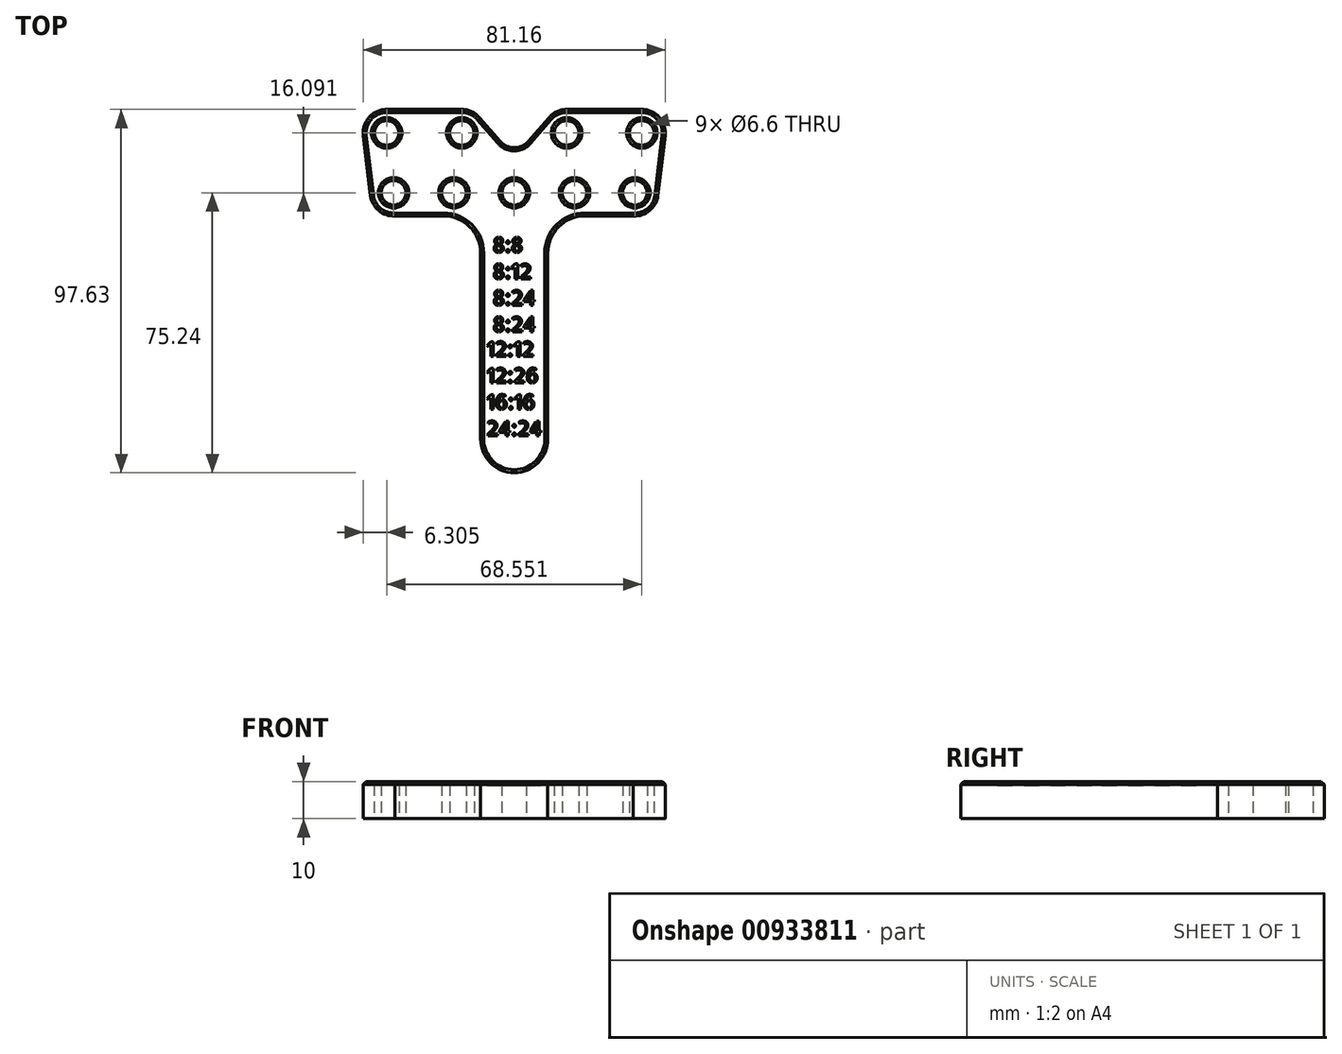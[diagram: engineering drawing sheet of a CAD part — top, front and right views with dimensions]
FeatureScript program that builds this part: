
annotation { "Feature Type Name" : "Feature", "Feature Type Description" : "" }
export const myFeature = defineFeature(function(context is Context, id is Id, definition is map)
    precondition{}
    {
        {
            var Q0;
            Q0=qCreatedBy(makeId("Top.planeOp"),FACE);
            var sketch = newSketch(context, id + "F0", { "sketchPlane" : qUnion([Q0])});
            skPoint(sketch, "E0.middle", {"position": v(0, 0) * mm});
            skCircle(sketch, "E1", {"center": v(0, 0) * mm, "radius": 3.3 * mm});
            skCircle(sketch, "E2", {"center": v(16.2, 0) * mm, "radius": 3.3 * mm});
            skCircle(sketch, "E3", {"center": v(32.4, 0) * mm, "radius": 3.3 * mm});
            skCircle(sketch, "E4.MirrorC", {"center": v(-16.2, 0) * mm, "radius": 3.3 * mm});
            skCircle(sketch, "E5.MirrorC", {"center": v(-32.4, 0) * mm, "radius": 3.3 * mm});
            skCircle(sketch, "E6", {"center": v(-32.4, 0) * mm, "radius": 16.2 * mm, "construction": true});
            skCircle(sketch, "E7", {"center": v(-16.2, 0) * mm, "radius": 24.2 * mm, "construction": true});
            skCircle(sketch, "E8", {"center": v(-34.28, -16.1) * mm, "radius": 3.3 * mm});
            skCircle(sketch, "E9", {"center": v(-14.08, -16.1) * mm, "radius": 3.3 * mm});
            skCircle(sketch, "E10.MirrorC", {"center": v(14.08, -16.1) * mm, "radius": 3.3 * mm});
            skCircle(sketch, "E11.MirrorC", {"center": v(34.28, -16.1) * mm, "radius": 3.3 * mm});
            skArc(sketch, "E12.0", {"start": v(14.08, -22.4) * mm, "mid": v(11.46, -21.82) * mm, "end": v(9.31, -20.21) * mm});
            skLineSegment(sketch, "E13.MirrorCS", {"start": v(9.31, -20.21) * mm, "end": v(3.78, -13.82) * mm});
            skArc(sketch, "E14.0", {"start": v(40.53, -15.34) * mm, "mid": v(38.99, -20.27) * mm, "end": v(34.28, -22.4) * mm});
            skArc(sketch, "E15", {"start": v(38.6, 0.74) * mm, "mid": v(36.4, 4.8) * mm, "end": v(32, 6.24) * mm});
            skLineSegment(sketch, "E16", {"start": v(14.08, -22.4) * mm, "end": v(34.28, -22.4) * mm});
            skLineSegment(sketch, "E17", {"start": v(40.53, -15.34) * mm, "end": v(38.6, 0.74) * mm});
            skArc(sketch, "E18.MirrorCS", {"start": v(-38.6, 0.74) * mm, "mid": v(-36.4, 4.8) * mm, "end": v(-32, 6.24) * mm});
            skLineSegment(sketch, "E19.MirrorCS", {"start": v(-40.53, -15.34) * mm, "end": v(-38.6, 0.74) * mm});
            skArc(sketch, "E20.MirrorCS", {"start": v(-40.53, -15.34) * mm, "mid": v(-38.99, -20.27) * mm, "end": v(-34.28, -22.4) * mm});
            skLineSegment(sketch, "E21.MirrorCS", {"start": v(-14.08, -22.4) * mm, "end": v(-34.28, -22.4) * mm});
            skArc(sketch, "E22.MirrorCS", {"start": v(-14.08, -22.4) * mm, "mid": v(-11.46, -21.82) * mm, "end": v(-9.31, -20.21) * mm});
            skLineSegment(sketch, "E23.MirrorCS", {"start": v(-9.31, -20.21) * mm, "end": v(-3.78, -13.82) * mm});
            skLineSegment(sketch, "E24", {"start": v(19, 6.24) * mm, "end": v(32, 6.24) * mm});
            skPoint(sketch, "E25.visualSharp", {"position": v(0, -9.45) * mm});
            skArc(sketch, "E25.filletArc", {"start": v(3.78, -13.82) * mm, "mid": v(0, -12.1) * mm, "end": v(-3.78, -13.82) * mm});
            skLineSegment(sketch, "E26", {"start": v(0, 6.24) * mm, "end": v(0, 66.24) * mm, "construction": true});
            skArc(sketch, "E27", {"start": v(9, 66.24) * mm, "mid": v(0, 75.24) * mm, "end": v(-9, 66.24) * mm});
            skLineSegment(sketch, "E28", {"start": v(9, 66.24) * mm, "end": v(9, 16.24) * mm});
            skLineSegment(sketch, "E29.MirrorCS", {"start": v(-9, 66.24) * mm, "end": v(-9, 16.24) * mm});
            skPoint(sketch, "E30.newPointA", {"position": v(9, 6.24) * mm});
            skPoint(sketch, "E30.newPointB", {"position": v(-32, 6.24) * mm});
            skArc(sketch, "E30.filletArc", {"start": v(9, 16.24) * mm, "mid": v(11.93, 9.17) * mm, "end": v(19, 6.24) * mm});
            skLineSegment(sketch, "E31", {"start": v(-32, 6.24) * mm, "end": v(-19, 6.24) * mm});
            skPoint(sketch, "E32.visualSharp", {"position": v(-9, 6.24) * mm});
            skArc(sketch, "E32.filletArc", {"start": v(-19, 6.24) * mm, "mid": v(-11.93, 9.17) * mm, "end": v(-9, 16.24) * mm});
            skLineSegment(sketch, "E33", {"start": v(0, 0) * mm, "end": v(0, 6.24) * mm, "construction": true});
            skSolve(sketch);
        }
        {
            var Q0;
            Q0 = qSketchRegion(id + "F0", true);
            extrude(context, id + "F1", {"entities" : qUnion([Q0]), "depth" : 10 * mm, "offsetDistance" : 25 * mm});
        }
        {
            var Q0;
            Q0=makeQuery(id+"F1.opExtrude","CAP_EDGE",EDGE,{"disambiguationData":[OSD([sQuery(id+"F0.wireOp",EDGE,"E5.MirrorC")])],"isStart":false});
            var Q1;
            Q1=makeQuery(id+"F1.opExtrude","CAP_EDGE",EDGE,{"disambiguationData":[OSD([sQuery(id+"F0.wireOp",EDGE,"E8")])],"isStart":false});
            var Q2;
            Q2=makeQuery(id+"F1.opExtrude","CAP_EDGE",EDGE,{"disambiguationData":[OSD([sQuery(id+"F0.wireOp",EDGE,"E4.MirrorC")])],"isStart":false});
            var Q3;
            Q3=makeQuery(id+"F1.opExtrude","CAP_EDGE",EDGE,{"disambiguationData":[OSD([sQuery(id+"F0.wireOp",EDGE,"E9")])],"isStart":false});
            var Q4;
            Q4=makeQuery(id+"F1.opExtrude","CAP_EDGE",EDGE,{"disambiguationData":[OSD([sQuery(id+"F0.wireOp",EDGE,"E1")])],"isStart":false});
            var Q5;
            Q5=makeQuery(id+"F1.opExtrude","CAP_EDGE",EDGE,{"disambiguationData":[OSD([sQuery(id+"F0.wireOp",EDGE,"E2")])],"isStart":false});
            var Q6;
            Q6=makeQuery(id+"F1.opExtrude","CAP_EDGE",EDGE,{"disambiguationData":[OSD([sQuery(id+"F0.wireOp",EDGE,"E10.MirrorC")])],"isStart":false});
            var Q7;
            Q7=makeQuery(id+"F1.opExtrude","CAP_EDGE",EDGE,{"disambiguationData":[OSD([sQuery(id+"F0.wireOp",EDGE,"E3")])],"isStart":false});
            var Q8;
            Q8=makeQuery(id+"F1.opExtrude","CAP_EDGE",EDGE,{"disambiguationData":[OSD([sQuery(id+"F0.wireOp",EDGE,"E11.MirrorC")])],"isStart":false});
            var Q9;
            Q9=makeQuery(id+"F1.opExtrude","CAP_FACE",FACE,{"disambiguationData":[OSD([sQuery(id+"F0.wireOp",EDGE,"E1"),sQuery(id+"F0.wireOp",EDGE,"E2"),sQuery(id+"F0.wireOp",EDGE,"E3"),sQuery(id+"F0.wireOp",EDGE,"E4.MirrorC"),sQuery(id+"F0.wireOp",EDGE,"E5.MirrorC"),sQuery(id+"F0.wireOp",EDGE,"E8"),sQuery(id+"F0.wireOp",EDGE,"E9"),sQuery(id+"F0.wireOp",EDGE,"E10.MirrorC"),sQuery(id+"F0.wireOp",EDGE,"E11.MirrorC"),sQuery(id+"F0.wireOp",EDGE,"E12.0"),sQuery(id+"F0.wireOp",EDGE,"E13.MirrorCS"),sQuery(id+"F0.wireOp",EDGE,"E14.0"),sQuery(id+"F0.wireOp",EDGE,"E15"),sQuery(id+"F0.wireOp",EDGE,"E16"),sQuery(id+"F0.wireOp",EDGE,"E17"),sQuery(id+"F0.wireOp",EDGE,"E18.MirrorCS"),sQuery(id+"F0.wireOp",EDGE,"E19.MirrorCS"),sQuery(id+"F0.wireOp",EDGE,"E20.MirrorCS"),sQuery(id+"F0.wireOp",EDGE,"E21.MirrorCS"),sQuery(id+"F0.wireOp",EDGE,"E22.MirrorCS"),sQuery(id+"F0.wireOp",EDGE,"E23.MirrorCS"),sQuery(id+"F0.wireOp",EDGE,"E24"),sQuery(id+"F0.wireOp",EDGE,"E25.filletArc"),sQuery(id+"F0.wireOp",EDGE,"E27"),sQuery(id+"F0.wireOp",EDGE,"E28"),sQuery(id+"F0.wireOp",EDGE,"E29.MirrorCS"),sQuery(id+"F0.wireOp",EDGE,"E30.filletArc"),sQuery(id+"F0.wireOp",EDGE,"E31"),sQuery(id+"F0.wireOp",EDGE,"E32.filletArc")])],"isStart":false});
            chamfer(context, id + "F2", {"entities" : qUnion([Q0, Q1, Q2, Q3, Q4, Q5, Q6, Q7, Q8, Q9]), "width" : .8 * mm, "tangentPropagation" : true});
        }
        {
            var Q0;
            Q0=makeQuery(id+"F1.opExtrude","SWEPT_BODY",BODY,{"disambiguationData":[OSD([sQuery(id+"F0.wireOp",EDGE,"E1"),sQuery(id+"F0.wireOp",EDGE,"E2"),sQuery(id+"F0.wireOp",EDGE,"E3"),sQuery(id+"F0.wireOp",EDGE,"E4.MirrorC"),sQuery(id+"F0.wireOp",EDGE,"E5.MirrorC"),sQuery(id+"F0.wireOp",EDGE,"E8"),sQuery(id+"F0.wireOp",EDGE,"E9"),sQuery(id+"F0.wireOp",EDGE,"E10.MirrorC"),sQuery(id+"F0.wireOp",EDGE,"E11.MirrorC"),sQuery(id+"F0.wireOp",EDGE,"E12.0"),sQuery(id+"F0.wireOp",EDGE,"E13.MirrorCS"),sQuery(id+"F0.wireOp",EDGE,"E14.0"),sQuery(id+"F0.wireOp",EDGE,"E15"),sQuery(id+"F0.wireOp",EDGE,"E16"),sQuery(id+"F0.wireOp",EDGE,"E17"),sQuery(id+"F0.wireOp",EDGE,"E18.MirrorCS"),sQuery(id+"F0.wireOp",EDGE,"E19.MirrorCS"),sQuery(id+"F0.wireOp",EDGE,"E20.MirrorCS"),sQuery(id+"F0.wireOp",EDGE,"E21.MirrorCS"),sQuery(id+"F0.wireOp",EDGE,"E22.MirrorCS"),sQuery(id+"F0.wireOp",EDGE,"E23.MirrorCS"),sQuery(id+"F0.wireOp",EDGE,"E24"),sQuery(id+"F0.wireOp",EDGE,"E25.filletArc"),sQuery(id+"F0.wireOp",EDGE,"E27"),sQuery(id+"F0.wireOp",EDGE,"E28"),sQuery(id+"F0.wireOp",EDGE,"E29.MirrorCS"),sQuery(id+"F0.wireOp",EDGE,"E30.filletArc"),sQuery(id+"F0.wireOp",EDGE,"E31"),sQuery(id+"F0.wireOp",EDGE,"E32.filletArc")])]});
            var Q1;
            Q1=makeQuery(id+"F1.opExtrude","SWEPT_FACE",FACE,{"disambiguationData":[OSD([sQuery(id+"F0.wireOp",EDGE,"E1")])]});
            transform(context, id + "F3", {"entities" : qUnion([Q0]), "transformType" : TransformType.ROTATION, "transformAxis" : qUnion([Q1]), "angle" : 180 * degree, "makeCopy" : false});
        }
        {
            var Q0;
            Q0=makeQuery(id+"F1.opExtrude","CAP_FACE",FACE,{"disambiguationData":[OSD([sQuery(id+"F0.wireOp",EDGE,"E1"),sQuery(id+"F0.wireOp",EDGE,"E2"),sQuery(id+"F0.wireOp",EDGE,"E3"),sQuery(id+"F0.wireOp",EDGE,"E4.MirrorC"),sQuery(id+"F0.wireOp",EDGE,"E5.MirrorC"),sQuery(id+"F0.wireOp",EDGE,"E8"),sQuery(id+"F0.wireOp",EDGE,"E9"),sQuery(id+"F0.wireOp",EDGE,"E10.MirrorC"),sQuery(id+"F0.wireOp",EDGE,"E11.MirrorC"),sQuery(id+"F0.wireOp",EDGE,"E12.0"),sQuery(id+"F0.wireOp",EDGE,"E13.MirrorCS"),sQuery(id+"F0.wireOp",EDGE,"E14.0"),sQuery(id+"F0.wireOp",EDGE,"E15"),sQuery(id+"F0.wireOp",EDGE,"E16"),sQuery(id+"F0.wireOp",EDGE,"E17"),sQuery(id+"F0.wireOp",EDGE,"E18.MirrorCS"),sQuery(id+"F0.wireOp",EDGE,"E19.MirrorCS"),sQuery(id+"F0.wireOp",EDGE,"E20.MirrorCS"),sQuery(id+"F0.wireOp",EDGE,"E21.MirrorCS"),sQuery(id+"F0.wireOp",EDGE,"E22.MirrorCS"),sQuery(id+"F0.wireOp",EDGE,"E23.MirrorCS"),sQuery(id+"F0.wireOp",EDGE,"E24"),sQuery(id+"F0.wireOp",EDGE,"E25.filletArc"),sQuery(id+"F0.wireOp",EDGE,"E27"),sQuery(id+"F0.wireOp",EDGE,"E28"),sQuery(id+"F0.wireOp",EDGE,"E29.MirrorCS"),sQuery(id+"F0.wireOp",EDGE,"E30.filletArc"),sQuery(id+"F0.wireOp",EDGE,"E31"),sQuery(id+"F0.wireOp",EDGE,"E32.filletArc")])],"isStart":false});
            var sketch = newSketch(context, id + "F4", { "sketchPlane" : qUnion([Q0])});
            skText(sketch, "E34", { "text": "8:8\n8:12\n8:24\n8:24", "fontName": "AllertaStencil-Regular.ttf"});
            skText(sketch, "E35", { "text": "12:12\n12:26\n16:16\n24:24\n\n", "fontName": "AllertaStencil-Regular.ttf"});
            const initialGuessF4  = {"E34": [-0.0058, -0.016, 1, 0, 0.004], "E35": [-0.0075, -0.044, 1, 0, 0.004]};
            skSetInitialGuess(sketch, initialGuessF4);
            skSolve(sketch);
        }
        {
            var Q0;
            Q0 = qSketchRegion(id + "F4", true);
            extrude(context, id + "F5", {"entities" : qUnion([Q0]), "operationType" : NewBodyOperationType.REMOVE, "oppositeDirection" : true, "depth" : 1 * mm, "offsetDistance" : 25 * mm});
        }
    });
